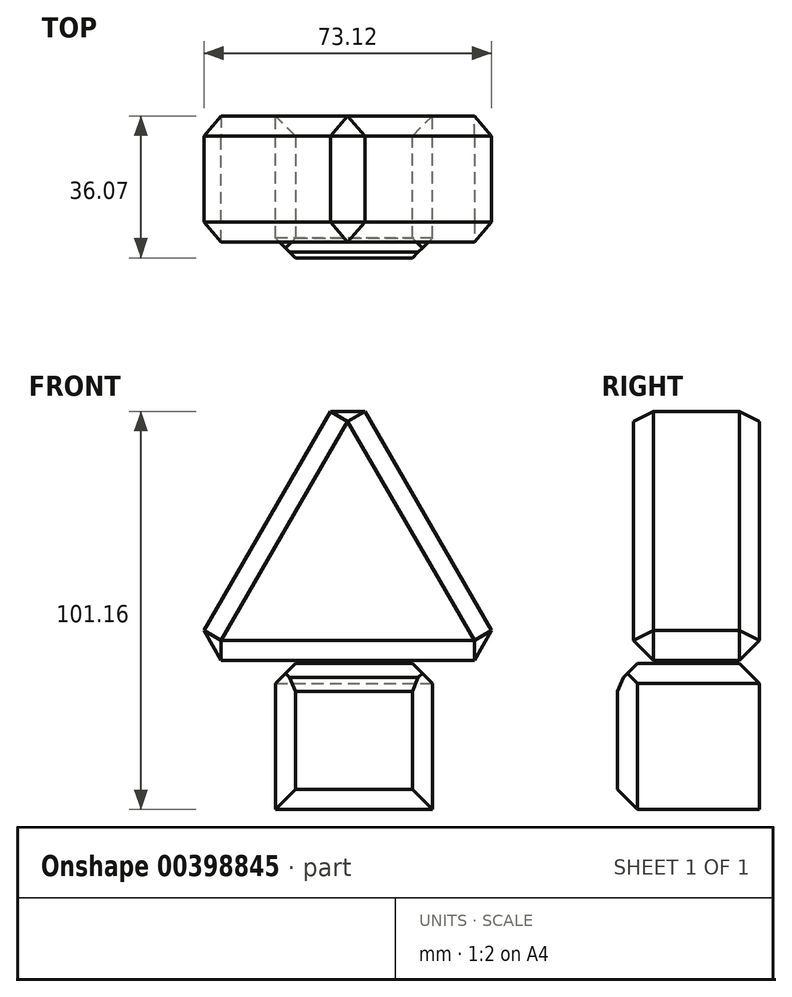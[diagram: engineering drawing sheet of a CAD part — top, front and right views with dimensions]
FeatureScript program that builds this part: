
annotation { "Feature Type Name" : "Feature", "Feature Type Description" : "" }
export const myFeature = defineFeature(function(context is Context, id is Id, definition is map)
    precondition{}
    {
        {
            var Q0;
            Q0=qCreatedBy(makeId("Front.planeOp"),FACE);
            var sketch = newSketch(context, id + "F0", { "sketchPlane" : qUnion([Q0])});
            skLineSegment(sketch, "E0.bottom", {"start": v(0, 0) * mm, "end": v(-39.83, 0) * mm});
            skLineSegment(sketch, "E0.top", {"start": v(0, 37.15) * mm, "end": v(-39.83, 37.15) * mm});
            skLineSegment(sketch, "E0.left", {"start": v(0, 0) * mm, "end": v(0, 37.15) * mm});
            skLineSegment(sketch, "E0.right", {"start": v(-39.83, 0) * mm, "end": v(-39.83, 37.15) * mm});
            skSolve(sketch);
        }
        {
            var Q0;
            Q0=makeQuery(id+"F0.imprint","IMPRINT",FACE,{"disambiguationData":[TD([[makeQuery(id+"F0.imprint","IMPRINT",EDGE,{"derivedFrom":sQuery(id+"F0.wireOp",EDGE,"E0.bottom")}),-1.0]])]});
            extrude(context, id + "F1", {"entities" : qUnion([Q0]), "depth" : 36.07 * mm});
        }
        {
            var Q0;
            Q0=makeQuery(id+"F1.opExtrude","SWEPT_FACE",FACE,{"disambiguationData":[OSD([sQuery(id+"F0.wireOp",EDGE,"E0.top")])]});
            chamfer(context, id + "F2", {"entities" : qUnion([Q0]), "width" : 5.08 * mm, "tangentPropagation" : true});
        }
        {
            var Q0;
            Q0=qCreatedBy(makeId("Front.planeOp"),FACE);
            var sketch = newSketch(context, id + "F3", { "sketchPlane" : qUnion([Q0])});
            skCircle(sketch, "E1.cCircle", {"center": v(-21.48, 61.49) * mm, "radius": 23.65 * mm, "construction": true});
            skLineSegment(sketch, "E1.0", {"start": v(19.48, 37.84) * mm, "end": v(-62.44, 37.84) * mm});
            skLineSegment(sketch, "E1.1", {"start": v(-62.44, 37.84) * mm, "end": v(-21.48, 108.78) * mm});
            skLineSegment(sketch, "E1.2", {"start": v(-21.48, 108.78) * mm, "end": v(19.48, 37.84) * mm});
            skPoint(sketch, "E1.0.midPoint", {"position": v(-21.48, 37.84) * mm});
            skSolve(sketch);
        }
        {
            var Q0;
            Q0=makeQuery(id+"F3.imprint","IMPRINT",FACE,{"disambiguationData":[TD([[makeQuery(id+"F3.imprint","IMPRINT",EDGE,{"derivedFrom":sQuery(id+"F3.wireOp",EDGE,"E1.0")}),-1.0]])]});
            extrude(context, id + "F4", {"entities" : qUnion([Q0]), "depth" : 32 * mm});
        }
        {
            var Q0;
            Q0=makeQuery(id+"F4.opExtrude","CAP_FACE",FACE,{"disambiguationData":[OSD([sQuery(id+"F3.wireOp",EDGE,"E1.0"),sQuery(id+"F3.wireOp",EDGE,"E1.1"),sQuery(id+"F3.wireOp",EDGE,"E1.2")])],"isStart":true});
            var Q1;
            Q1=makeQuery(id+"F4.opExtrude","SWEPT_FACE",FACE,{"disambiguationData":[OSD([sQuery(id+"F3.wireOp",EDGE,"E1.2")])]});
            var Q2;
            Q2=makeQuery(id+"F4.opExtrude","SWEPT_FACE",FACE,{"disambiguationData":[OSD([sQuery(id+"F3.wireOp",EDGE,"E1.1")])]});
            var Q3;
            Q3=makeQuery(id+"F4.opExtrude","CAP_FACE",FACE,{"disambiguationData":[OSD([sQuery(id+"F3.wireOp",EDGE,"E1.0"),sQuery(id+"F3.wireOp",EDGE,"E1.1"),sQuery(id+"F3.wireOp",EDGE,"E1.2")])],"isStart":false});
            chamfer(context, id + "F5", {"entities" : qUnion([Q0, Q1, Q2, Q3]), "width" : 5.08 * mm, "tangentPropagation" : true});
        }
        {
            var Q0;
            Q0=makeQuery(id+"F1.opExtrude","CAP_FACE",FACE,{"disambiguationData":[OSD([sQuery(id+"F0.wireOp",EDGE,"E0.bottom"),sQuery(id+"F0.wireOp",EDGE,"E0.top"),sQuery(id+"F0.wireOp",EDGE,"E0.left"),sQuery(id+"F0.wireOp",EDGE,"E0.right")])],"isStart":false});
            chamfer(context, id + "F6", {"entities" : qUnion([Q0]), "width" : 5.08 * mm, "tangentPropagation" : true});
        }
    });
